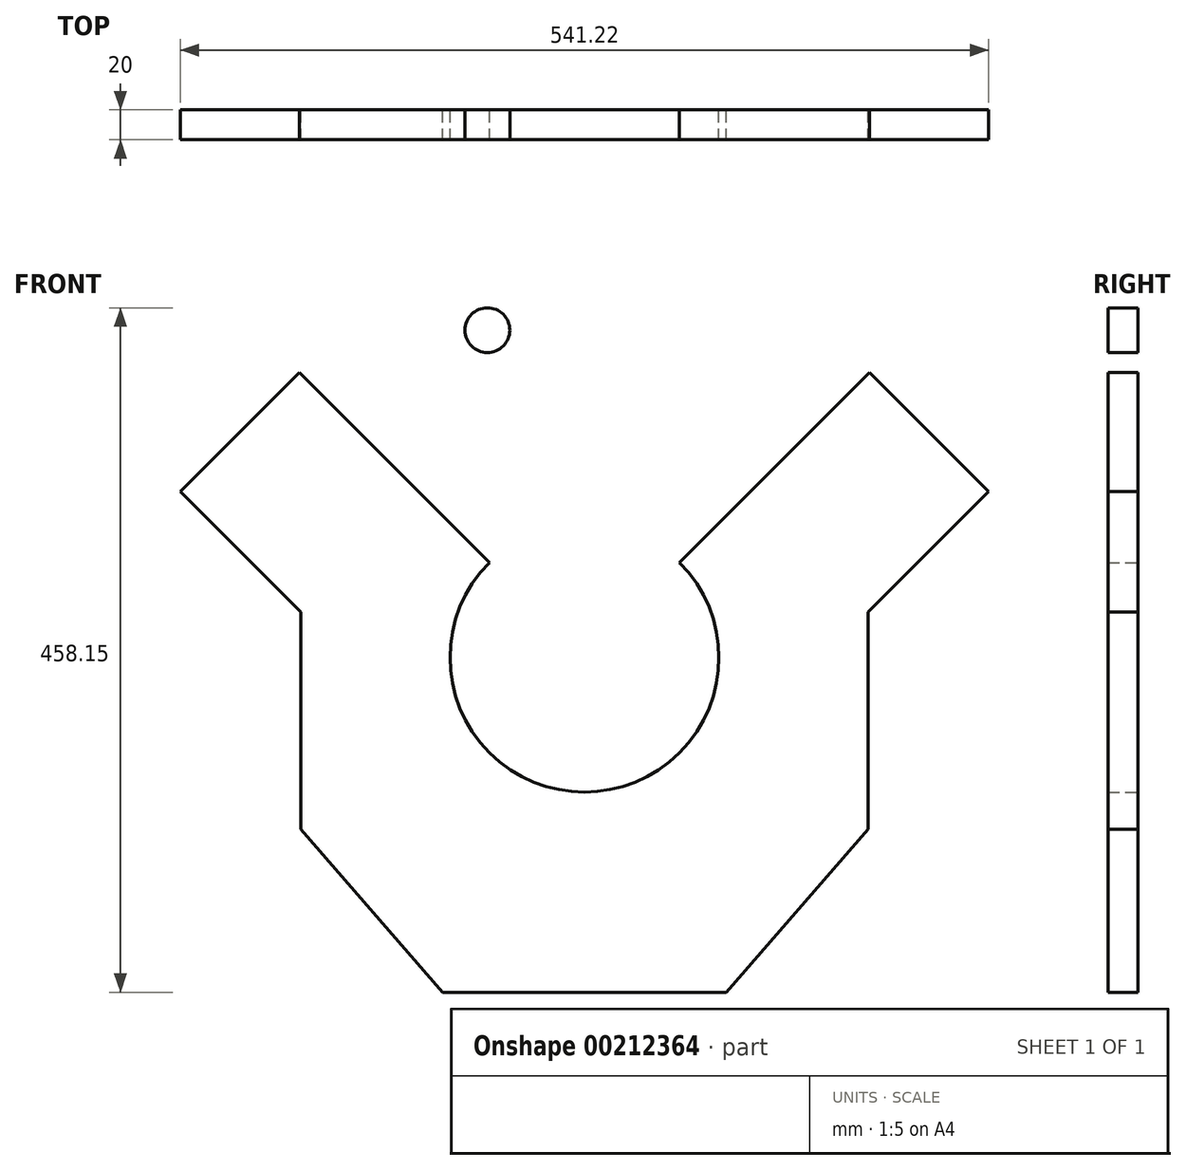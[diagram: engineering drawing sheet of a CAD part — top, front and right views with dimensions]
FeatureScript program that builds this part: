
annotation { "Feature Type Name" : "Feature", "Feature Type Description" : "" }
export const myFeature = defineFeature(function(context is Context, id is Id, definition is map)
    precondition{}
    {
        {
            var Q0;
            Q0=qCreatedBy(makeId("Front.planeOp"),FACE);
            var sketch = newSketch(context, id + "F0", { "sketchPlane" : qUnion([Q0])});
            skCircle(sketch, "E0", {"center": v(0, -64.78) * mm, "radius": 80 * mm});
            skCircle(sketch, "E1", {"center": v(0, -64.78) * mm, "radius": 10 * mm});
            skCircle(sketch, "E2", {"center": v(0, -64.78) * mm, "radius": 30 * mm});
            skCircle(sketch, "E3", {"center": v(-65, 154.37) * mm, "radius": 15 * mm});
            skLineSegment(sketch, "E4", {"start": v(-190, -179.78) * mm, "end": v(-94.8, -288.78) * mm});
            skLineSegment(sketch, "E5", {"start": v(-190, -34.26) * mm, "end": v(-190, -179.78) * mm});
            skLineSegment(sketch, "E6", {"start": v(-190, -34.26) * mm, "end": v(-270.61, 46.36) * mm});
            skLineSegment(sketch, "E7", {"start": v(-270.61, 46.36) * mm, "end": v(-79.86, 237.11) * mm});
            skLineSegment(sketch, "E8", {"start": v(-79.86, 237.11) * mm, "end": v(0, 237.11) * mm});
            skLineSegment(sketch, "E9", {"start": v(0, -288.78) * mm, "end": v(-94.8, -288.78) * mm});
            skLineSegment(sketch, "E10", {"start": v(79.86, 237.11) * mm, "end": v(0, 237.11) * mm});
            skLineSegment(sketch, "E11", {"start": v(270.61, 46.36) * mm, "end": v(79.86, 237.11) * mm});
            skLineSegment(sketch, "E12", {"start": v(190, -34.26) * mm, "end": v(270.61, 46.36) * mm});
            skLineSegment(sketch, "E13", {"start": v(190, -34.26) * mm, "end": v(190, -179.78) * mm});
            skLineSegment(sketch, "E14", {"start": v(190, -179.78) * mm, "end": v(94.8, -288.78) * mm});
            skLineSegment(sketch, "E15", {"start": v(0, -288.78) * mm, "end": v(94.8, -288.78) * mm});
            skCircle(sketch, "E16", {"center": v(65, 154.37) * mm, "radius": 15 * mm});
            skLineSegment(sketch, "E17", {"start": v(0, -64.78) * mm, "end": v(353.55, 288.78) * mm});
            skLineSegment(sketch, "E18", {"start": v(0, -64.78) * mm, "end": v(-353.55, 288.78) * mm});
            skCircle(sketch, "E19", {"center": v(0, -64.78) * mm, "radius": 90 * mm});
            skSolve(sketch);
        }
        {
            var Q0;
            Q0=makeQuery(id+"F0.imprint","IMPRINT",FACE,{"disambiguationData":[TD([[makeQuery(id+"F0.imprint","IMPRINT",EDGE,{"derivedFrom":sQuery(id+"F0.wireOp",EDGE,"E3")}),1.0]])]});
            var Q1;
            Q1=makeQuery(id+"F0.imprint","IMPRINT",FACE,{"disambiguationData":[TD([[makeQuery(id+"F0.imprint","IMPRINT",EDGE,{"derivedFrom":sQuery(id+"F0.wireOp",EDGE,"E4")}),1.0]])]});
            extrude(context, id + "F1", {"entities" : qUnion([Q0, Q1]), "depth" : 20 * mm});
        }
    });
